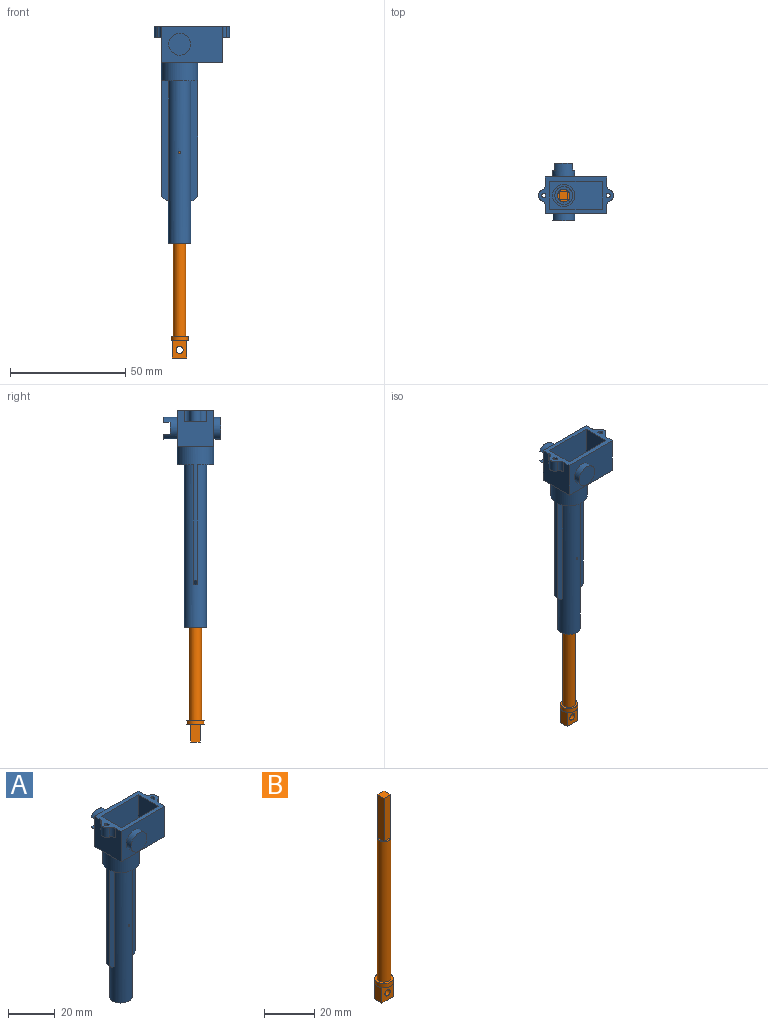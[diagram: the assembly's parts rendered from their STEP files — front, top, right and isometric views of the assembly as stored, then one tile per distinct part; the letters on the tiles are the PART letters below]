
ASSEMBLY  parts=2 mates=1
PART A: 53 faces, bbox 32.6x25x94.3 mm
  f0: cylinder r=4.85mm len=70.5mm, axis (0,0,1), area 1937.3mm2, adj f1,f18,f21,f43,f44,f45,f46,f47
  f1: plane 15.67x6.9mm, normal (0,0,-1), area 55mm2, adj f0,f15,f43,f47
  f2: plane 16x15.8mm, normal (1,0,0), area 215.1mm2, adj f8,f9,f11,f12,f38,f40,f41,f42
  f3: plane 16x15.8mm, normal (-1,0,0), area 215.1mm2, adj f8,f9,f11,f12,f34,f35,f36,f37
  f4: plane 9.5x7mm, normal (0,1,0), area 52.6mm2, adj f24,f25,f26,f27,f29,f30,f31
  f5: plane 22.6x13.8mm, normal (0,1,0), area 311.9mm2, adj f6,f10,f11,f13
  f6: plane 13.8x12.1mm, normal (1,0,0), area 167mm2, adj f5,f7,f11,f13
  f7: plane 22.6x13.8mm, normal (0,-1,0), area 311.9mm2, adj f6,f10,f11,f13
  f8: plane 26.5x15.8mm, normal (0,-1,0), area 347.8mm2, adj f2,f3,f11,f12,f22
  f9: plane 26.5x15.8mm, normal (0,1,0), area 347.8mm2, adj f2,f3,f11,f12,f24
  f10: plane 13.8x12.1mm, normal (-1,0,0), area 167mm2, adj f5,f7,f11,f13
  f11: plane 32.6x16mm, normal (0,0,1), area 173.4mm2, adj f2,f3,f5,f6,f7,f8,f9,f10
  f12: plane 26.5x16mm, normal (0,0,-1), area 227.9mm2, adj f2,f3,f8,f9,f15
  f13: plane 22.6x12.1mm, normal (0,0,1), area 199.6mm2, adj f5,f6,f7,f10,f14
  f14: cylinder r=4.85mm len=9.7mm, axis (0,0,-1), area 213.3mm2, adj f13,f16
  f15: cylinder r=7.9mm len=58mm, axis (0,0,1), area 597.6mm2, adj f1,f12,f18,f43,f44,f46,f47,f49
  f16: plane 9.7x9.7mm, normal (0,0,1), area 27.3mm2, adj f14,f17
  f17: cylinder r=3.85mm len=39mm, axis (0,0,1), area 941.9mm2, adj f16,f19,f51,f52
  f18: plane 15.67x6.9mm, normal (0,0,-1), area 55mm2, adj f0,f15,f44,f46
  f19: plane 7.7x7.7mm, normal (0,0,1), area 22.8mm2, adj f17,f20
  f20: cylinder r=2.75mm len=34.5mm, axis (0,0,1), area 596.1mm2, adj f19,f21
  f21: plane 9.7x9.7mm, normal (0,0,-1), area 50.1mm2, adj f0,f20
  f22: cylinder r=4.75mm len=9.5mm, axis (0,1,0), area 89.5mm2, adj f8,f23
  f23: plane 9.5x9.5mm, normal (0,-1,0), area 70.9mm2, adj f22
  f24: cylinder r=4.75mm len=9.5mm, axis (0,-1,0), area 146.7mm2, adj f4,f9,f25,f27,f28,f29,f30,f32
  f25: plane 3x1.72mm, normal (-0.05,0,-1), area 5.2mm2, adj f4,f24,f26,f28
  f26: cylinder r=3.5mm len=4.57mm, axis (0,-1,0), area 14.9mm2, adj f4,f25,f27,f28
  f27: plane 3x1.72mm, normal (0.05,0,-1), area 5.2mm2, adj f4,f24,f26,f28
  f28: plane 8.01x2.19mm, normal (0,1,0), area 9.1mm2, adj f24,f25,f26,f27
  f29: plane 3x1.72mm, normal (-0.05,0,1), area 5.2mm2, adj f4,f24,f31,f32
  f30: plane 3x1.72mm, normal (0.05,0,1), area 5.2mm2, adj f4,f24,f31,f32
  f31: cylinder r=3.5mm len=4.57mm, axis (0,-1,0), area 14.9mm2, adj f4,f29,f30,f32
  f32: plane 8.01x2.19mm, normal (0,1,0), area 9.1mm2, adj f24,f29,f30,f31
  f33: cylinder r=2.5mm len=5mm, axis (0,0,1), area 29.3mm2, adj f11,f35,f36,f37
  f34: cylinder r=1mm len=5mm, axis (0,0,1), area 21.5mm2, adj f3,f11,f35
  f35: plane 9.21x3.05mm, normal (0,0,-1), area 11.4mm2, adj f3,f33,f34,f36,f37
  f36: cylinder r=2.5mm len=5mm, axis (0,0,1), area 14.6mm2, adj f3,f11,f33,f35
  f37: cylinder r=2.5mm len=5mm, axis (0,0,1), area 14.6mm2, adj f3,f11,f33,f35
  f38: cylinder r=1mm len=5mm, axis (0,0,1), area 21.5mm2, adj f2,f11,f40
  f39: cylinder r=2.5mm len=5mm, axis (0,0,1), area 29.3mm2, adj f11,f40,f41,f42
  f40: plane 9.21x3.05mm, normal (0,0,-1), area 11.4mm2, adj f2,f38,f39,f41,f42
  f41: cylinder r=2.5mm len=5mm, axis (0,0,1), area 14.6mm2, adj f2,f11,f39,f40
  f42: cylinder r=2.5mm len=5mm, axis (0,0,1), area 14.6mm2, adj f2,f11,f39,f40
  f43: plane 52.04x3.13mm, normal (0,-1,0), area 158.7mm2, adj f0,f1,f15,f45,f50
  f44: plane 52.04x3.13mm, normal (0,1,0), area 158.7mm2, adj f0,f15,f18,f45,f50
  f45: plane 2x1.15mm, normal (0,0,-1), area 2.1mm2, adj f0,f43,f44,f50
  f46: plane 52.04x3.13mm, normal (0,1,0), area 158.7mm2, adj f0,f15,f18,f48,f49
  f47: plane 52.04x3.13mm, normal (0,-1,0), area 158.7mm2, adj f0,f1,f15,f48,f49
  f48: plane 2x1.15mm, normal (0,0,-1), area 2.1mm2, adj f0,f46,f47,f49
  f49: cone r=5.9mm half-angle=45deg, axis (0,0,1), area 5.8mm2, adj f15,f46,f47,f48
  f50: cone r=5.9mm half-angle=45deg, axis (0,0,1), area 5.8mm2, adj f15,f43,f44,f45
  f51: cylinder r=0.5mm len=1mm, axis (0,-1,0), area 3.1mm2, adj f0,f17
  f52: cylinder r=0.5mm len=1mm, axis (0,-1,0), area 3.1mm2, adj f0,f17
PART B: 19 faces, bbox 7.5x7.5x99 mm
  f0: plane 6.34x1.75mm, normal (0,0,-1), area 7.8mm2, adj f10,f13
  f1: plane 4x0.58mm, normal (0,0,-1), area 1.6mm2, adj f10,f16
  f2: plane 6.34x1.75mm, normal (0,0,-1), area 7.8mm2, adj f10,f15
  f3: plane 21x3.55mm, normal (0,-1,0), area 74.5mm2, adj f4,f6,f7,f9
  f4: plane 21x3.55mm, normal (1,0,0), area 74.5mm2, adj f3,f5,f7,f9
  f5: plane 21x3.55mm, normal (0,1,0), area 74.5mm2, adj f4,f6,f7,f9
  f6: plane 21x3.55mm, normal (-1,0,0), area 74.5mm2, adj f3,f5,f7,f9
  f7: plane 3.55x3.55mm, normal (0,0,1), area 12.6mm2, adj f3,f4,f5,f6
  f8: cylinder r=2.7mm len=68.5mm, axis (0,0,1), area 1162.1mm2, adj f9,f12
  f9: plane 5.4x5.4mm, normal (0,0,1), area 10.3mm2, adj f3,f4,f5,f6,f8
  f10: cylinder r=3.75mm len=7.5mm, axis (0,0,1), area 47.1mm2, adj f0,f1,f2,f11,f12
  f11: plane 4x0.58mm, normal (0,0,-1), area 1.6mm2, adj f10,f14
  f12: plane 7.5x7.5mm, normal (0,0,1), area 21.3mm2, adj f8,f10
  f13: plane 7.5x6.34mm, normal (0,1,0), area 40.5mm2, adj f0,f14,f16,f17,f18
  f14: plane 7.5x4mm, normal (1,0,0), area 30mm2, adj f11,f13,f15,f17
  f15: plane 7.5x6.34mm, normal (0,-1,0), area 40.5mm2, adj f2,f14,f16,f17,f18
  f16: plane 7.5x4mm, normal (-1,0,0), area 30mm2, adj f1,f13,f15,f17
  f17: plane 6.34x4mm, normal (0,0,-1), area 25.4mm2, adj f13,f14,f15,f16
  f18: cylinder r=1.5mm len=4mm, axis (0,-1,0), area 37.7mm2, adj f13,f15
PLACE A t=(14.52,-35.01,28.27)mm
PLACE B t=(14.52,-35.01,22.06)mm
MATE slider A.f20 <-> B.f8  axis (0,0,1) through (9.17,-35.01,-15.73)mm
